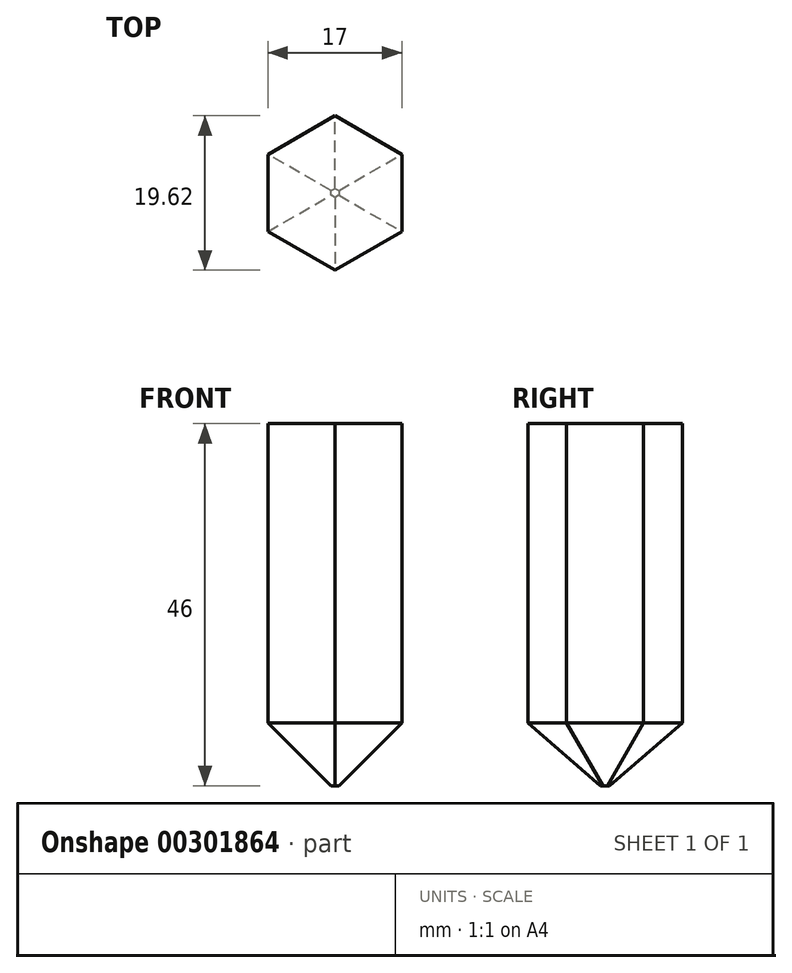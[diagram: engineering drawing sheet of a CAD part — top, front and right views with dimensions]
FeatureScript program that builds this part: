
annotation { "Feature Type Name" : "Feature", "Feature Type Description" : "" }
export const myFeature = defineFeature(function(context is Context, id is Id, definition is map)
    precondition{}
    {
        {
            var Q0;
            Q0=qCreatedBy(makeId("Top.planeOp"),FACE);
            var sketch = newSketch(context, id + "F0", { "sketchPlane" : qUnion([Q0])});
            skCircle(sketch, "E0.cCircle", {"center": v(0, 0) * mm, "radius": 8.5 * mm, "construction": true});
            skLineSegment(sketch, "E0.0", {"start": v(8.5, -4.9) * mm, "end": v(0, -9.81) * mm});
            skLineSegment(sketch, "E0.1", {"start": v(0, -9.81) * mm, "end": v(-8.5, -4.9) * mm});
            skLineSegment(sketch, "E0.2", {"start": v(-8.5, -4.9) * mm, "end": v(-8.5, 4.9) * mm});
            skLineSegment(sketch, "E0.3", {"start": v(-8.5, 4.9) * mm, "end": v(0, 9.81) * mm});
            skLineSegment(sketch, "E0.4", {"start": v(0, 9.81) * mm, "end": v(8.5, 4.9) * mm});
            skLineSegment(sketch, "E0.5", {"start": v(8.5, 4.9) * mm, "end": v(8.5, -4.9) * mm});
            skPoint(sketch, "E0.0.midPoint", {"position": v(4.25, -7.36) * mm});
            skSolve(sketch);
        }
        {
            var Q0;
            Q0=makeQuery(id+"F0.imprint","IMPRINT",FACE,{"disambiguationData":[TD([[makeQuery(id+"F0.imprint","IMPRINT",EDGE,{"derivedFrom":sQuery(id+"F0.wireOp",EDGE,"E0.0")}),-1.0]])]});
            extrude(context, id + "F1", {"entities" : qUnion([Q0]), "depth" : 46 * mm});
        }
        {
            var Q0;
            Q0=makeQuery(id+"F1.opExtrude","CAP_EDGE",EDGE,{"disambiguationData":[OSD([sQuery(id+"F0.wireOp",EDGE,"E0.0")])],"isStart":true});
            var Q1;
            Q1=makeQuery(id+"F1.opExtrude","CAP_EDGE",EDGE,{"disambiguationData":[OSD([sQuery(id+"F0.wireOp",EDGE,"E0.1")])],"isStart":true});
            var Q2;
            Q2=makeQuery(id+"F1.opExtrude","CAP_EDGE",EDGE,{"disambiguationData":[OSD([sQuery(id+"F0.wireOp",EDGE,"E0.3")])],"isStart":true});
            var Q3;
            Q3=makeQuery(id+"F1.opExtrude","CAP_EDGE",EDGE,{"disambiguationData":[OSD([sQuery(id+"F0.wireOp",EDGE,"E0.2")])],"isStart":true});
            var Q4;
            Q4=makeQuery(id+"F1.opExtrude","CAP_EDGE",EDGE,{"disambiguationData":[OSD([sQuery(id+"F0.wireOp",EDGE,"E0.4")])],"isStart":true});
            var Q5;
            Q5=makeQuery(id+"F1.opExtrude","CAP_EDGE",EDGE,{"disambiguationData":[OSD([sQuery(id+"F0.wireOp",EDGE,"E0.5")])],"isStart":true});
            chamfer(context, id + "F2", {"entities" : qUnion([Q0, Q1, Q2, Q3, Q4, Q5]), "width" : 8 * mm, "tangentPropagation" : true});
        }
    });
